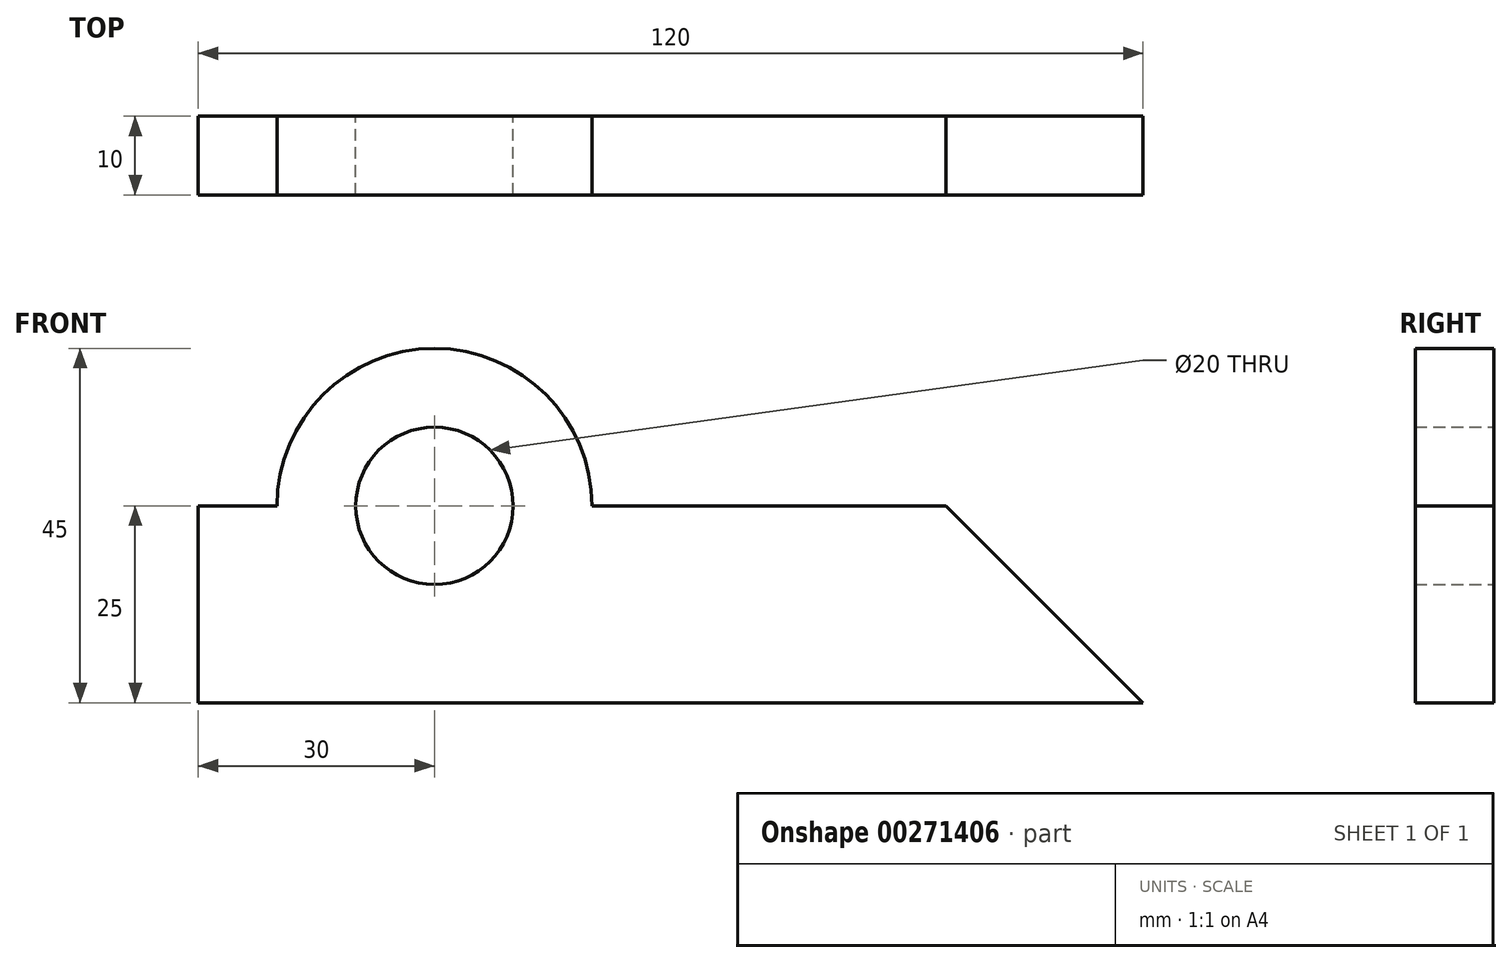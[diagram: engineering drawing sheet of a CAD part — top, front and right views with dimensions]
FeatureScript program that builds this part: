
annotation { "Feature Type Name" : "Feature", "Feature Type Description" : "" }
export const myFeature = defineFeature(function(context is Context, id is Id, definition is map)
    precondition{}
    {
        {
            var Q0;
            Q0=qCreatedBy(makeId("Front.planeOp"),FACE);
            var sketch = newSketch(context, id + "F0", { "sketchPlane" : qUnion([Q0])});
            skLineSegment(sketch, "E0", {"start": v(0, 0) * mm, "end": v(0, 25) * mm});
            skLineSegment(sketch, "E1", {"start": v(0, 25) * mm, "end": v(10, 25) * mm});
            skArc(sketch, "E2", {"start": v(50, 25) * mm, "mid": v(30, 45) * mm, "end": v(10, 25) * mm});
            skLineSegment(sketch, "E3", {"start": v(50, 25) * mm, "end": v(95, 25) * mm});
            skLineSegment(sketch, "E4", {"start": v(95, 25) * mm, "end": v(120, 0) * mm});
            skLineSegment(sketch, "E5", {"start": v(120, 0) * mm, "end": v(0, 0) * mm});
            skCircle(sketch, "E6", {"center": v(30, 25) * mm, "radius": 10 * mm});
            skSolve(sketch);
        }
        {
            var Q0;
            Q0 = qSketchRegion(id + "F0", true);
            extrude(context, id + "F1", {"entities" : qUnion([Q0]), "depth" : 10 * mm});
        }
    });
